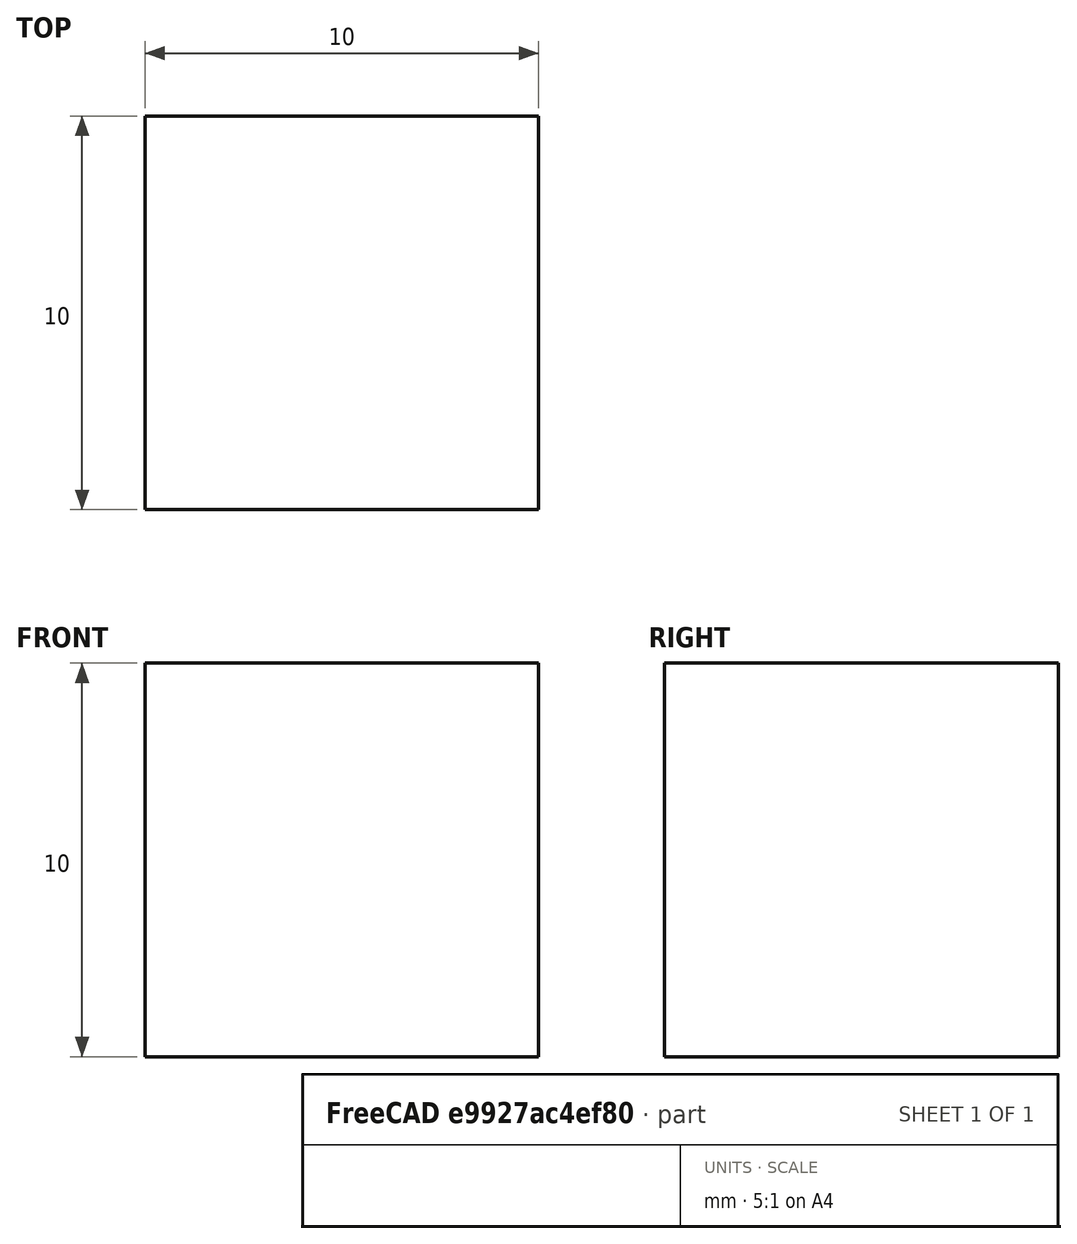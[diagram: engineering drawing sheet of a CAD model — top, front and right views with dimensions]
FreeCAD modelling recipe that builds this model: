
FCSTD DOCUMENT  (FreeCAD 0.18.4R)
Label: Mesure_cube_10mm
License: CC-BY 3.0
LicenseURL: http://creativecommons.org/licenses/by/3.0/
objects: Sketcher::SketchObject×1, PartDesign::Pad×1
note: 3 computed .brp shape members not serialized (recipe doc carries the construction recipe); baked Part::Feature solids carry a one-line shape summary decoded from their .brp

FEATURE [Sketcher::SketchObject] Sketch
  MapMode = 5
  sketch-geometry (4):
    g0: LineSegment StartX=-5 StartY=5 StartZ=0 EndX=5 EndY=5 EndZ=0
    g1: LineSegment StartX=5 StartY=5 StartZ=0 EndX=5 EndY=-5 EndZ=0
    g2: LineSegment StartX=5 StartY=-5 StartZ=0 EndX=-5 EndY=-5 EndZ=0
    g3: LineSegment StartX=-5 StartY=-5 StartZ=0 EndX=-5 EndY=5 EndZ=0
  constraints (10):
    c: Coincident(g0,g1)
    c: Coincident(g1,g2)
    c: Coincident(g2,g3)
    c: Coincident(g3,g0)
    c: Horizontal(g2)
    c: Vertical(g1)
    c: DistanceX(g0) = 10
    c: Equal(g0,g1)
    c: Symmetric(g0,g0,g-2)
    c: Symmetric(g0,g2,g-1)
FEATURE [PartDesign::Pad] Pad
  Length = 10
  Length2 = 100
  Profile = -> Sketch
  Type = 0
